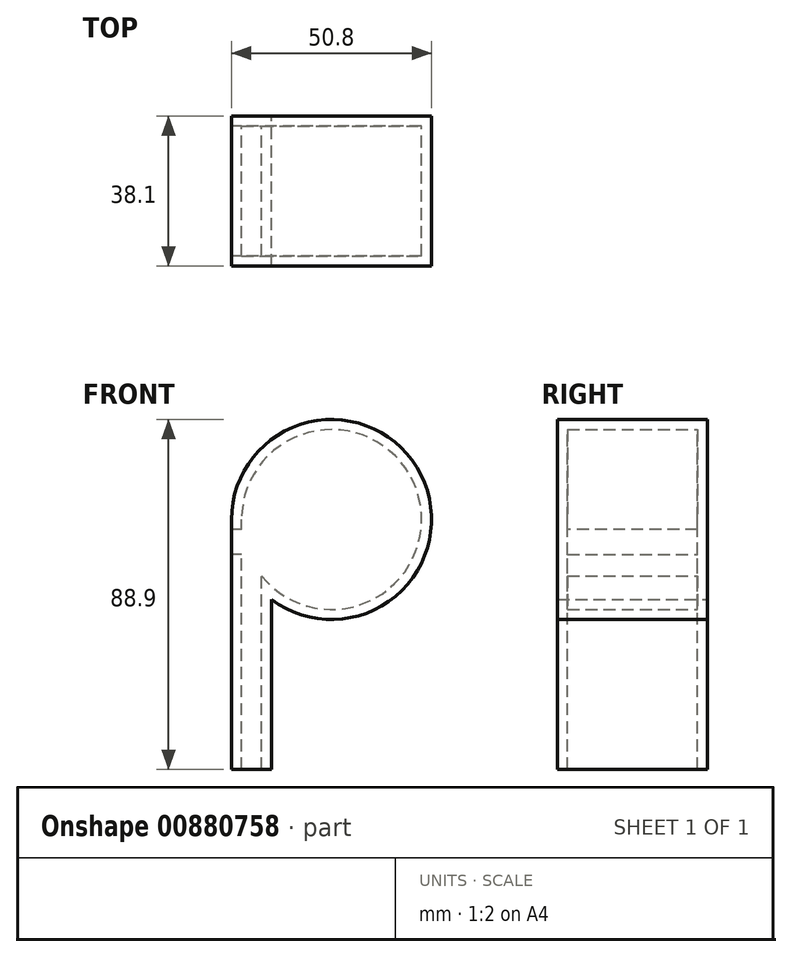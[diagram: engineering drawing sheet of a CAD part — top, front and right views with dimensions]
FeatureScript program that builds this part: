
annotation { "Feature Type Name" : "Feature", "Feature Type Description" : "" }
export const myFeature = defineFeature(function(context is Context, id is Id, definition is map)
    precondition{}
    {
        {
            var Q0;
            Q0=qCreatedBy(makeId("Front.planeOp"),FACE);
            var sketch = newSketch(context, id + "F0", { "sketchPlane" : qUnion([Q0])});
            skLineSegment(sketch, "E0", {"start": v(-25.4, -63.5) * mm, "end": v(-15.24, -63.5) * mm});
            skLineSegment(sketch, "E1", {"start": v(-25.4, -63.5) * mm, "end": v(-25.4, 0) * mm});
            skLineSegment(sketch, "E2", {"start": v(-15.24, -63.5) * mm, "end": v(-15.24, -20.32) * mm});
            skArc(sketch, "E3.converted", {"start": v(-25.4, 0) * mm, "mid": v(22.72, 11.36) * mm, "end": v(-15.24, -20.32) * mm});
            skPoint(sketch, "E4.orphan", {"position": v(25.4, 0) * mm});
            skSolve(sketch);
        }
        {
            var Q0;
            Q0 = qSketchRegion(id + "F0", true);
            extrude(context, id + "F1", {"entities" : qUnion([Q0]), "depth" : 38.1 * mm, "offsetDistance" : 25.4 * mm});
        }
        {
            var Q0;
            Q0=makeQuery(id+"F1.opExtrude","SWEPT_FACE",FACE,{"disambiguationData":[OSD([sQuery(id+"F0.wireOp",EDGE,"E0")])]});
            shell(context, id + "F2", {"entities" : qUnion([Q0]), "thickness" : 2.54 * mm});
        }
        {
            var Q0;
            Q0=makeQuery(id+"F1.opExtrude","SWEPT_FACE",FACE,{"disambiguationData":[OSD([sQuery(id+"F0.wireOp",EDGE,"E1")])]});
            var sketch = newSketch(context, id + "F3", { "sketchPlane" : qUnion([Q0])});
            skLineSegment(sketch, "E5.bottom", {"start": v(2.54, -8.9) * mm, "end": v(35.56, -8.89) * mm});
            skLineSegment(sketch, "E5.top", {"start": v(2.54, -2.54) * mm, "end": v(35.56, -2.54) * mm});
            skLineSegment(sketch, "E5.left", {"start": v(2.54, -8.9) * mm, "end": v(2.54, -2.54) * mm});
            skLineSegment(sketch, "E5.right", {"start": v(35.56, -8.89) * mm, "end": v(35.56, -2.54) * mm});
            skSolve(sketch);
        }
        {
            var Q0;
            Q0 = qSketchRegion(id + "F3", true);
            extrude(context, id + "F4", {"entities" : qUnion([Q0]), "operationType" : NewBodyOperationType.REMOVE, "endBound" : BoundingType.UP_TO_NEXT, "oppositeDirection" : true, "depth" : 25.4 * mm, "offsetDistance" : 25.4 * mm});
        }
    });
